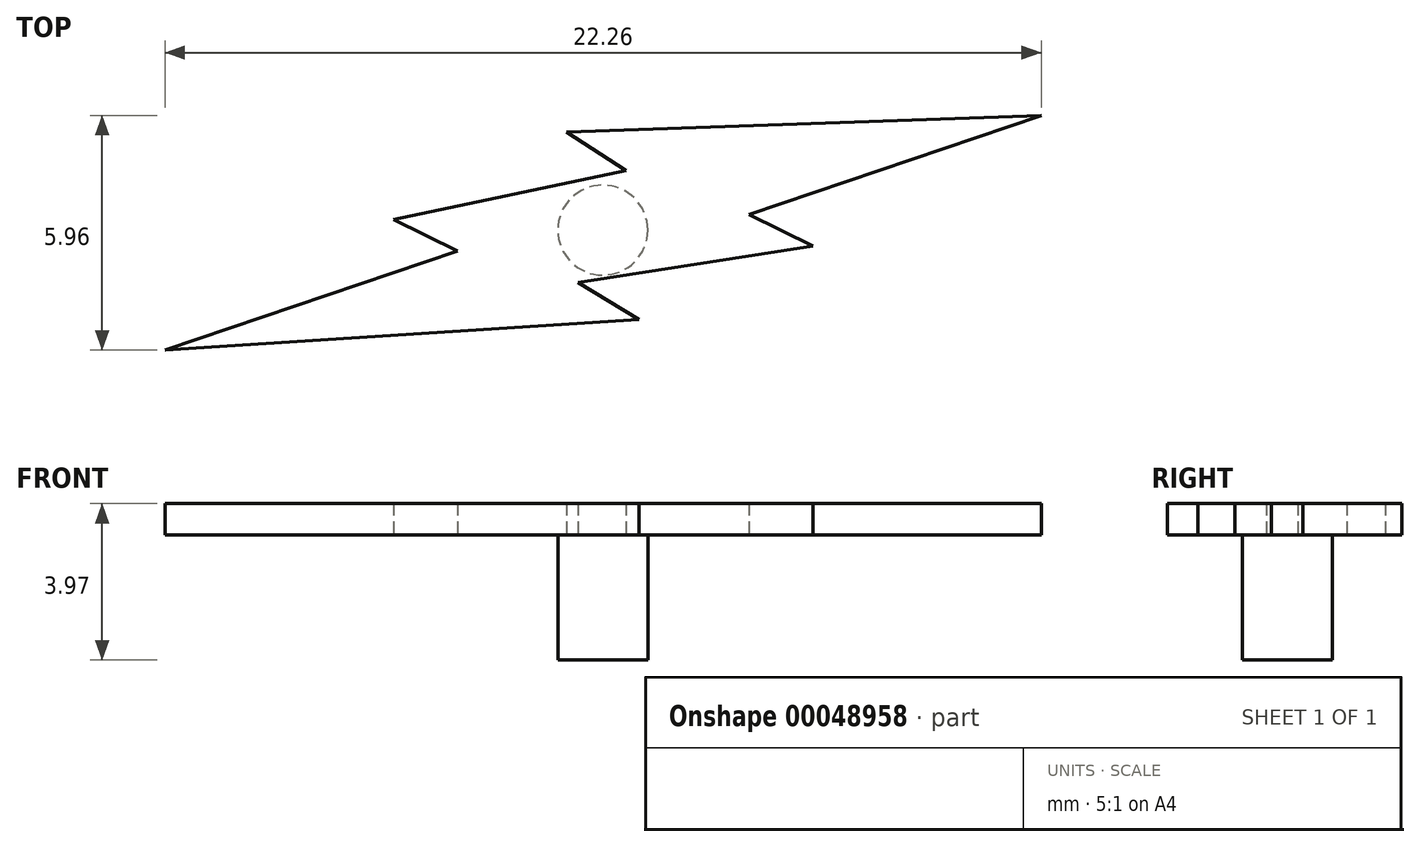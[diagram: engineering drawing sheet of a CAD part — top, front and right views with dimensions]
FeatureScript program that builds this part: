
annotation { "Feature Type Name" : "Feature", "Feature Type Description" : "" }
export const myFeature = defineFeature(function(context is Context, id is Id, definition is map)
    precondition{}
    {
        {
            var Q0;
            Q0=qCreatedBy(makeId("Top.planeOp"),FACE);
            var sketch = newSketch(context, id + "F0", { "sketchPlane" : qUnion([Q0])});
            skLineSegment(sketch, "E0", {"start": v(-11.12, -3.05) * mm, "end": v(0.92, -2.27) * mm});
            skLineSegment(sketch, "E1", {"start": v(-11.12, -3.05) * mm, "end": v(-3.7, -0.53) * mm});
            skLineSegment(sketch, "E2", {"start": v(0.92, -2.27) * mm, "end": v(-0.63, -1.33) * mm});
            skLineSegment(sketch, "E3", {"start": v(-3.7, -0.53) * mm, "end": v(-5.32, 0.27) * mm});
            skLineSegment(sketch, "E4", {"start": v(-0.63, -1.33) * mm, "end": v(5.33, -0.41) * mm});
            skLineSegment(sketch, "E5", {"start": v(5.33, -0.41) * mm, "end": v(3.71, 0.4) * mm});
            skLineSegment(sketch, "E6", {"start": v(3.71, 0.4) * mm, "end": v(11.14, 2.9) * mm});
            skLineSegment(sketch, "E7", {"start": v(-5.32, 0.27) * mm, "end": v(0.58, 1.52) * mm});
            skLineSegment(sketch, "E8", {"start": v(11.14, 2.9) * mm, "end": v(-0.92, 2.5) * mm});
            skLineSegment(sketch, "E9", {"start": v(0.58, 1.52) * mm, "end": v(-0.92, 2.5) * mm});
            skSolve(sketch);
        }
        {
            var Q0;
            Q0=makeQuery(id+"F0.imprint","IMPRINT",FACE,{"disambiguationData":[TD([[makeQuery(id+"F0.imprint","IMPRINT",EDGE,{"derivedFrom":sQuery(id+"F0.wireOp",EDGE,"E0")}),1.0]])]});
            extrude(context, id + "F1", {"entities" : qUnion([Q0]), "depth" : 0.8 * mm});
        }
        {
            var Q0;
            Q0=makeQuery(id+"F0.imprint","IMPRINT",FACE,{"disambiguationData":[TD([[makeQuery(id+"F0.imprint","IMPRINT",EDGE,{"derivedFrom":sQuery(id+"F0.wireOp",EDGE,"E0")}),1.0]])]});
            var sketch = newSketch(context, id + "F2", { "sketchPlane" : qUnion([Q0])});
            skCircle(sketch, "E10", {"center": v(0, 0) * mm, "radius": 1.14 * mm});
            skSolve(sketch);
        }
        {
            var Q0;
            Q0=makeQuery(id+"F2.imprint","IMPRINT",FACE,{"disambiguationData":[TD([[makeQuery(id+"F2.imprint","IMPRINT",EDGE,{"derivedFrom":sQuery(id+"F2.wireOp",EDGE,"E10")}),1.0]])]});
            extrude(context, id + "F3", {"entities" : qUnion([Q0]), "operationType" : NewBodyOperationType.ADD, "oppositeDirection" : true, "depth" : 3.17 * mm});
        }
    });
